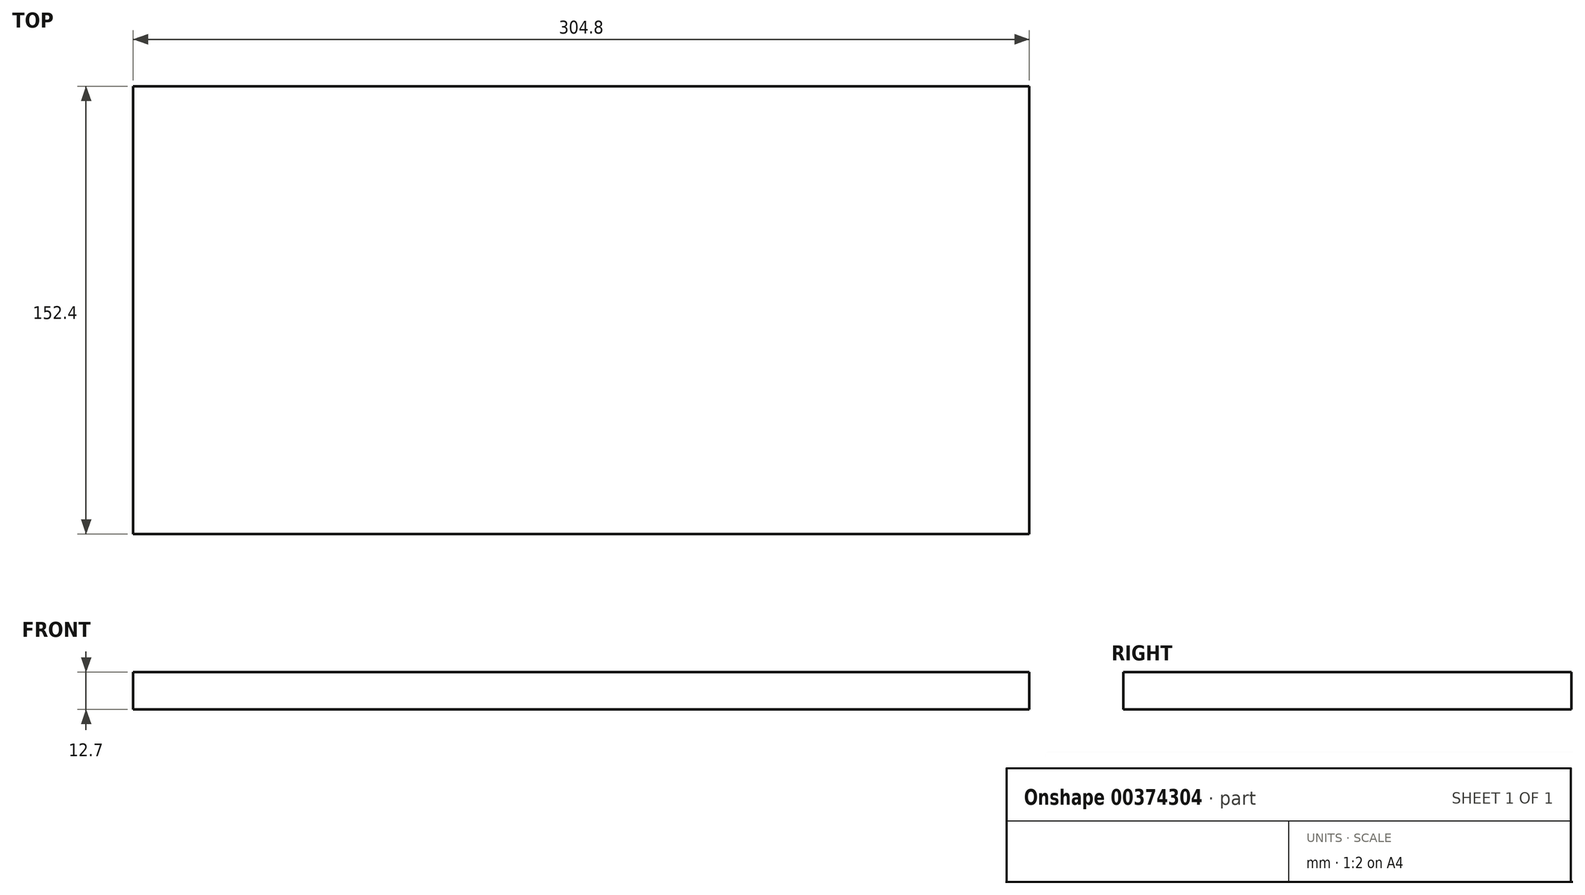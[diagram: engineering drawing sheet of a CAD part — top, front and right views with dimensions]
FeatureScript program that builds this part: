
annotation { "Feature Type Name" : "Feature", "Feature Type Description" : "" }
export const myFeature = defineFeature(function(context is Context, id is Id, definition is map)
    precondition{}
    {
        {
            var Q0;
            Q0=qCreatedBy(makeId("Top.planeOp"),FACE);
            var sketch = newSketch(context, id + "F0", { "sketchPlane" : qUnion([Q0])});
            skLineSegment(sketch, "E0.bottom", {"start": v(0, 0) * mm, "end": v(304.8, 0) * mm});
            skLineSegment(sketch, "E0.top", {"start": v(0, 152.4) * mm, "end": v(304.8, 152.4) * mm});
            skLineSegment(sketch, "E0.left", {"start": v(0, 0) * mm, "end": v(0, 152.4) * mm});
            skLineSegment(sketch, "E0.right", {"start": v(304.8, 0) * mm, "end": v(304.8, 152.4) * mm});
            skSolve(sketch);
        }
        {
            var Q0;
            Q0=makeQuery(id+"F0.imprint","IMPRINT",FACE,{"disambiguationData":[TD([[makeQuery(id+"F0.imprint","IMPRINT",EDGE,{"derivedFrom":sQuery(id+"F0.wireOp",EDGE,"E0.bottom")}),1.0]])]});
            extrude(context, id + "F1", {"entities" : qUnion([Q0]), "depth" : 12.7 * mm, "offsetDistance" : 25.4 * mm});
        }
    });
